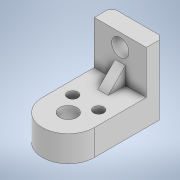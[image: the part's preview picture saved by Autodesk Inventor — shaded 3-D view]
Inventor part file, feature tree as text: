
AUTODESK INVENTOR PART (.ipt)
format: ipt  version: 2022 (Build 260153000, 153)  size: 152,064 bytes
history: native  units: mm
features: sketch x5, extrude x4, other x2
ambient origin geometry x8: Origin, YZ Plane, XZ Plane, XY Plane, X Axis, Y Axis, Z Axis, Center Point
bodies: Body1 (feature_tree)
feature tree (11):
  other  "Твердое тело1"
  extrude  "Выдавливание1"  Depth=80.0mm
  extrude  "Выдавливание2"  Depth=20.0mm
  extrude  "Выдавливание3"  Depth=12.0mm
  other  "РабПлоскость1"
  extrude  "Выдавливание4"  Depth=12.0mm
  sketch  "Эскиз7"
  sketch  "Эскиз1"
  sketch  "Эскиз2"
  sketch  "Эскиз3"
  sketch  "Эскиз6"
